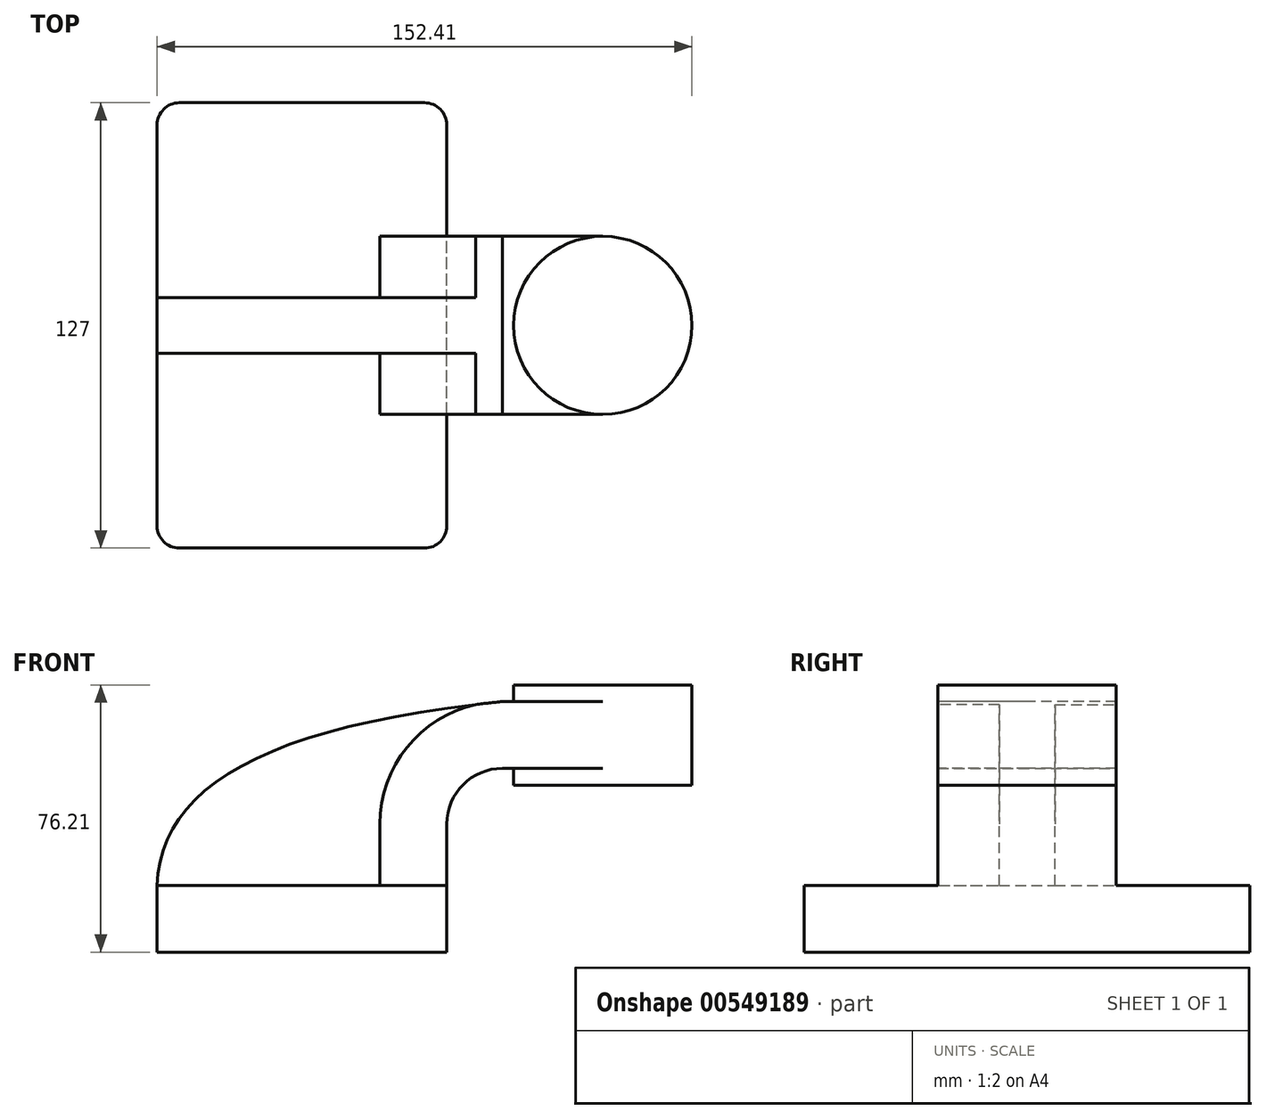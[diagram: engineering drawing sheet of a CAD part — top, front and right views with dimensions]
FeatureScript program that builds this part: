
annotation { "Feature Type Name" : "Feature", "Feature Type Description" : "" }
export const myFeature = defineFeature(function(context is Context, id is Id, definition is map)
    precondition{}
    {
        {
            var Q0;
            Q0=qCreatedBy(makeId("Front.planeOp"),FACE);
            var sketch = newSketch(context, id + "F0", { "sketchPlane" : qUnion([Q0])});
            skLineSegment(sketch, "E0.bottom", {"start": v(-41.27, -9.53) * mm, "end": v(41.28, -9.53) * mm});
            skLineSegment(sketch, "E0.top", {"start": v(-41.28, 9.52) * mm, "end": v(41.28, 9.52) * mm});
            skLineSegment(sketch, "E0.left", {"start": v(-41.28, -9.53) * mm, "end": v(-41.28, 9.53) * mm});
            skLineSegment(sketch, "E0.right", {"start": v(41.28, -9.53) * mm, "end": v(41.28, 9.52) * mm});
            skPoint(sketch, "E0.middle", {"position": v(0, 0) * mm});
            skLineSegment(sketch, "E1.bottom", {"start": v(60.33, 38.1) * mm, "end": v(111.12, 38.1) * mm});
            skLineSegment(sketch, "E1.top", {"start": v(60.33, 66.68) * mm, "end": v(111.12, 66.68) * mm});
            skLineSegment(sketch, "E1.left", {"start": v(60.33, 38.1) * mm, "end": v(60.33, 66.67) * mm});
            skLineSegment(sketch, "E1.right", {"start": v(111.13, 38.1) * mm, "end": v(111.12, 66.67) * mm});
            skPoint(sketch, "E1.middle", {"position": v(85.72, 52.39) * mm});
            skLineSegment(sketch, "E2", {"start": v(41.27, 9.52) * mm, "end": v(41.27, 27) * mm});
            skArc(sketch, "E3", {"start": v(41.27, 27) * mm, "mid": v(45.92, 38.23) * mm, "end": v(57.15, 42.88) * mm});
            skLineSegment(sketch, "E4", {"start": v(57.15, 42.88) * mm, "end": v(85.72, 42.88) * mm});
            skLineSegment(sketch, "E5.0", {"start": v(57.15, 61.93) * mm, "end": v(85.73, 61.93) * mm});
            skArc(sketch, "E5.1", {"start": v(22.22, 27) * mm, "mid": v(32.45, 51.7) * mm, "end": v(57.15, 61.93) * mm});
            skLineSegment(sketch, "E5.2", {"start": v(22.22, 9.52) * mm, "end": v(22.22, 27) * mm});
            skPoint(sketch, "E6", {"position": v(85.73, 38.1) * mm});
            skLineSegment(sketch, "E7", {"start": v(85.73, 38.1) * mm, "end": v(85.73, 66.67) * mm});
            skFitSpline(sketch, "E8", {"points": [v(-41.28, 9.53) * mm, v(57.15, 61.93) * mm], "startDerivative": vector(2.74, 82.86) * mm, "endDerivative": vector(205.26, 20.93) * mm});
            skSolve(sketch);
        }
        {
            var Q0;
            Q0=makeQuery(id+"F0.imprint","IMPRINT",FACE,{"disambiguationData":[TD([[makeQuery(id+"F0.imprint","IMPRINT",EDGE,{"derivedFrom":sQuery(id+"F0.wireOp",EDGE,"E0.bottom")}),1.0]])]});
            extrude(context, id + "F1", {"entities" : qUnion([Q0]), "endBound" : BoundingType.SYMMETRIC, "depth" : 127 * mm, "offsetDistance" : 25.4 * mm});
        }
        {
            var Q0;
            {var subQ0=sQuery(id+"F0.wireOp",EDGE,"E4");var subQ1=sQuery(id+"F0.wireOp",EDGE,"E1.left");var subQ2=makeQuery(id+"F0.imprint","INTERSECT",VERTEX,{"derivedFrom":[subQ1,subQ0]});Q0=makeQuery(id+"F0.imprint","IMPRINT",FACE,{"disambiguationData":[TD([[makeQuery(id+"F0.imprint","IMPRINT",EDGE,{"disambiguationData":[TD([[subQ2,-1.0]])],"derivedFrom":subQ1}),-1.0]])]});}
            var Q1;
            {var subQ1=sQuery(id+"F0.wireOp",EDGE,"E2");Q1=makeQuery(id+"F0.imprint","IMPRINT",FACE,{"disambiguationData":[TD([[makeQuery(id+"F0.imprint","IMPRINT",EDGE,{"derivedFrom":subQ1}),1.0]])]});}
            extrude(context, id + "F2", {"entities" : qUnion([Q0, Q1]), "operationType" : NewBodyOperationType.ADD, "endBound" : BoundingType.SYMMETRIC, "depth" : 50.8 * mm, "offsetDistance" : 25.4 * mm});
        }
        {
            var Q0;
            {var subQ3=sQuery(id+"F0.wireOp",EDGE,"E5.2");Q0=makeQuery(id+"F0.imprint","IMPRINT",FACE,{"disambiguationData":[TD([[makeQuery(id+"F0.imprint","IMPRINT",EDGE,{"derivedFrom":subQ3}),1.0]])]});}
            extrude(context, id + "F3", {"entities" : qUnion([Q0]), "operationType" : NewBodyOperationType.ADD, "endBound" : BoundingType.SYMMETRIC, "depth" : 15.88 * mm, "offsetDistance" : 25.4 * mm});
        }
        {
            var Q0;
            {var subQ4=sQuery(id+"F0.wireOp",EDGE,"E1.right");Q0=makeQuery(id+"F0.imprint","IMPRINT",FACE,{"disambiguationData":[TD([[makeQuery(id+"F0.imprint","IMPRINT",EDGE,{"derivedFrom":subQ4}),1.0]])]});}
            var Q1;
            Q1=sQuery(id+"F0.wireOp",EDGE,"E7");
            revolve(context, id + "F4", {"operationType" : NewBodyOperationType.ADD, "entities" : qUnion([Q0]), "axis" : qUnion([Q1]), "revolveType" : RevolveType.FULL});
        }
        {
            var Q0;
            Q0=makeQuery(id+"F1.opExtrude","CAP_EDGE",EDGE,{"disambiguationData":[OSD([sQuery(id+"F0.wireOp",EDGE,"E0.left")])],"isStart":false});
            var Q1;
            Q1=makeQuery(id+"F1.opExtrude","CAP_EDGE",EDGE,{"disambiguationData":[OSD([sQuery(id+"F0.wireOp",EDGE,"E0.right")])],"isStart":false});
            var Q2;
            Q2=makeQuery(id+"F1.opExtrude","CAP_EDGE",EDGE,{"disambiguationData":[OSD([sQuery(id+"F0.wireOp",EDGE,"E0.right")])],"isStart":true});
            var Q3;
            Q3=makeQuery(id+"F1.opExtrude","CAP_EDGE",EDGE,{"disambiguationData":[OSD([sQuery(id+"F0.wireOp",EDGE,"E0.left")])],"isStart":true});
            fillet(context, id + "F5", {"entities" : qUnion([Q0, Q1, Q2, Q3]), "radius" : 6.35 * mm, "tangentPropagation" : true, "allowEdgeOverflow" : false});
        }
    });
